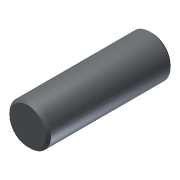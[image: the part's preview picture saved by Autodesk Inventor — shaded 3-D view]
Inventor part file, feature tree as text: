
AUTODESK INVENTOR PART (.ipt)
format: ipt  version: 2013 (Build 170138000, 138)  size: 74,752 bytes
history: native  units: in
note: dims shown in document units (in); Inventor stores cm internally (conversion verified against a paired STEP export)
features: chamfer x1, other x1, imported_body x1
ambient origin geometry x8: Origin, YZ Plane, XZ Plane, XY Plane, X Axis, Y Axis, Z Axis, Center Point
feature tree (3):
  chamfer  "Chamfer1"  [1 undecoded]
  other  "217-2625-010 Rev11"
  imported_body  "Base1"
note: 1 required parameter value undecoded (feature->parameter linkage not recoverable at this tier; creation-order binding heuristic only, values carry confidence <= 0.55)
